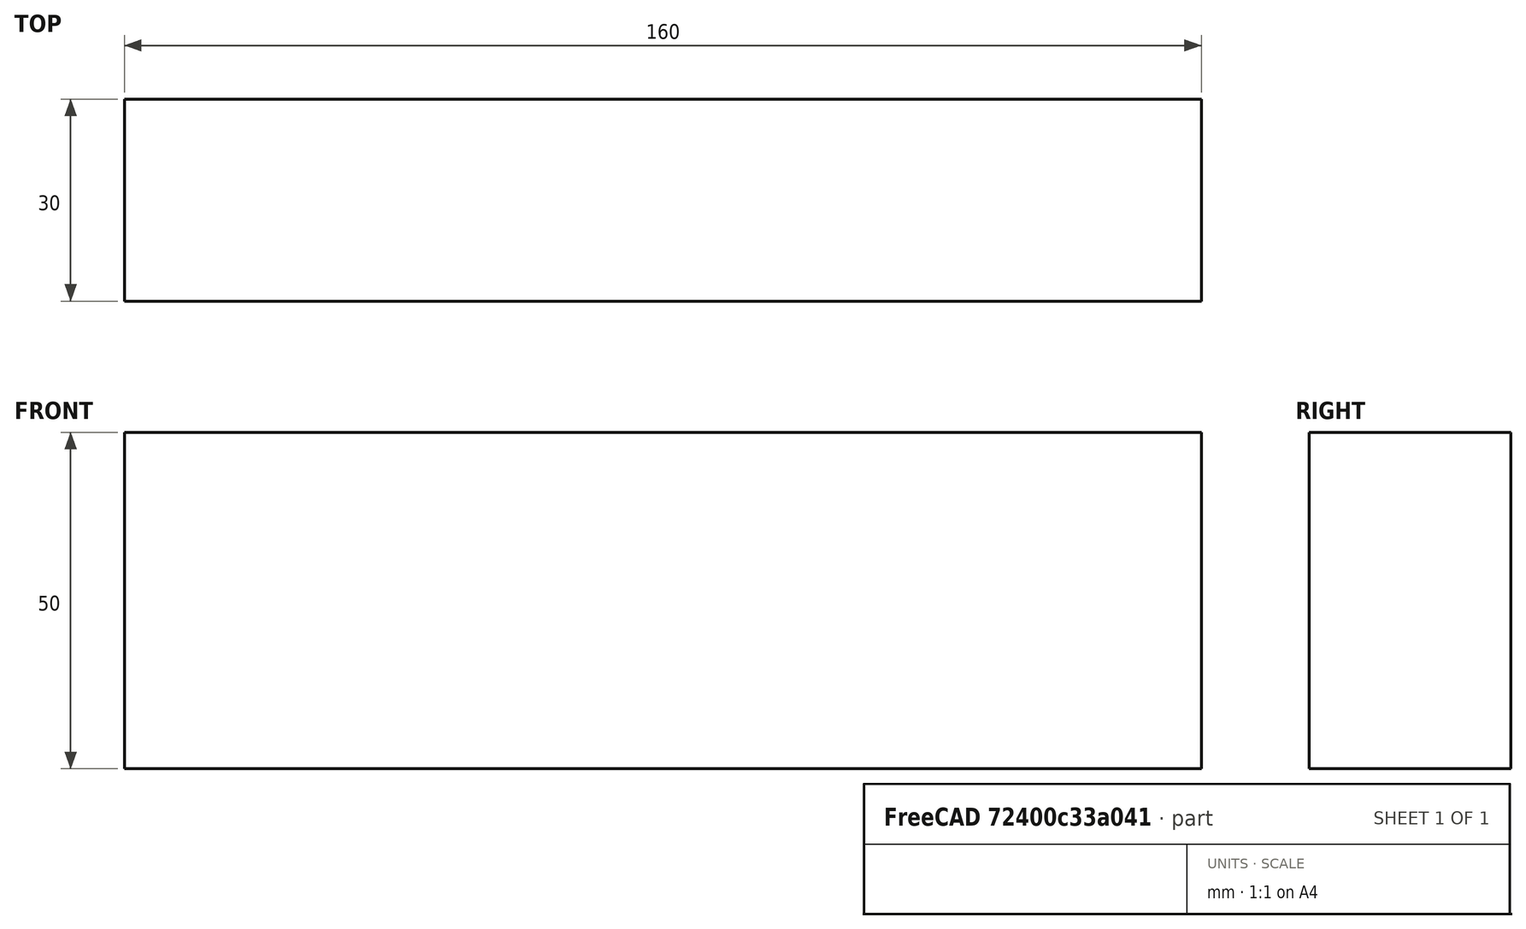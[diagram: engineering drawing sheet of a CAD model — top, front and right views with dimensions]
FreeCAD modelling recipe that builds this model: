
FCSTD DOCUMENT  (FreeCAD 0.15R4671 (Git))
Label: Flat Bar 160x30 EN10058 S235JR
License: All rights reserved
LicenseURL: http://en.wikipedia.org/wiki/All_rights_reserved
objects: Sketcher::SketchObject×1, Part::Extrusion×1
note: 2 computed .brp shape members not serialized (recipe doc carries the construction recipe); baked Part::Feature solids carry a one-line shape summary decoded from their .brp

FEATURE [Sketcher::SketchObject] Sketch
  sketch-geometry (4):
    g0: LineSegment StartX=-80 StartY=-15 StartZ=0 EndX=80 EndY=-15 EndZ=0
    g1: LineSegment StartX=80 StartY=-15 StartZ=0 EndX=80 EndY=15 EndZ=0
    g2: LineSegment StartX=80 StartY=15 StartZ=0 EndX=-80 EndY=15 EndZ=0
    g3: LineSegment StartX=-80 StartY=15 StartZ=0 EndX=-80 EndY=-15 EndZ=0
  constraints (12):
    c: Coincident(g0,g1)
    c: Coincident(g1,g2)
    c: Coincident(g2,g3)
    c: Coincident(g3,g0)
    c: Horizontal(g0)
    c: Horizontal(g2)
    c: Vertical(g1)
    c: Vertical(g3)
    c: Symmetric(g1,g2,g-2)
    c: Symmetric(g0,g1,g-1)
    c: DistanceY(g1) = 30
    c: DistanceX(g0) = 160
FEATURE [Part::Extrusion] Extrude  label="Flat Bar 160x30 EN10058 S235JR"
  Base = -> Sketch
  Dir = (0,0,50)
  Solid = true
